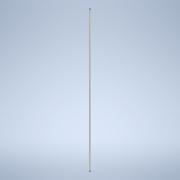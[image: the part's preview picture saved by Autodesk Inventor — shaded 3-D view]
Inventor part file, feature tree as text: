
AUTODESK INVENTOR PART (.ipt)
format: ipt  version: 2022 (Build 260153000, 153)  size: 90,624 bytes
history: native  units: mm
features: extrude x1, sketch x1
ambient origin geometry x8: Origin, YZ Plane, XZ Plane, XY Plane, X Axis, Y Axis, Z Axis, Center Point
bodies: Solid1 (feature_tree)
feature tree (2):
  extrude  "Extrusion1"  Depth=1000.0mm TaperAngle=0.0deg
  sketch  "Sketch1"  dims[d0=9.0mm d1=1000.0mm d2=0.0mm]
